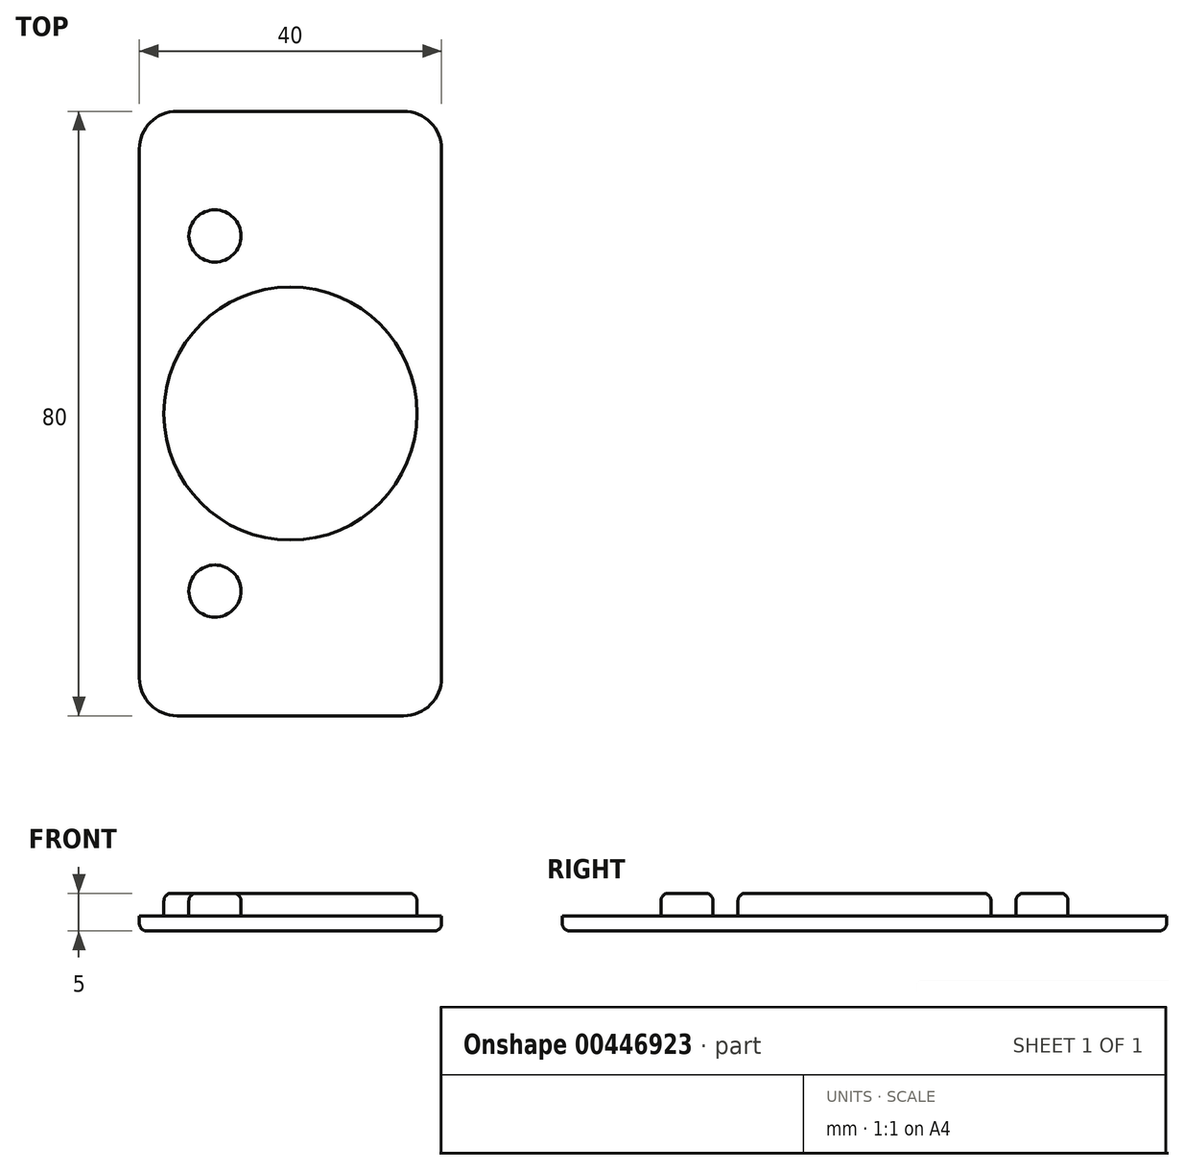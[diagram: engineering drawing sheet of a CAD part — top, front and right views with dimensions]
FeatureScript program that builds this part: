
annotation { "Feature Type Name" : "Feature", "Feature Type Description" : "" }
export const myFeature = defineFeature(function(context is Context, id is Id, definition is map)
    precondition{}
    {
        {
            var Q0;
            Q0=qCreatedBy(makeId("Top.planeOp"),FACE);
            var sketch = newSketch(context, id + "F0", { "sketchPlane" : qUnion([Q0])});
            skLineSegment(sketch, "E0.bottom", {"start": v(15, -40) * mm, "end": v(-15, -40) * mm});
            skLineSegment(sketch, "E0.top", {"start": v(15, 40) * mm, "end": v(-15, 40) * mm});
            skLineSegment(sketch, "E0.left", {"start": v(20, -35) * mm, "end": v(20, 35) * mm});
            skLineSegment(sketch, "E0.right", {"start": v(-20, -35) * mm, "end": v(-20, 35) * mm});
            skPoint(sketch, "E0.middle", {"position": v(0, 0) * mm});
            skPoint(sketch, "E1.visualSharp", {"position": v(20, -40) * mm});
            skArc(sketch, "E1.filletArc", {"start": v(15, -40) * mm, "mid": v(18.54, -38.54) * mm, "end": v(20, -35) * mm});
            skPoint(sketch, "E2.visualSharp", {"position": v(-20, -40) * mm});
            skArc(sketch, "E2.filletArc", {"start": v(-20, -35) * mm, "mid": v(-18.54, -38.54) * mm, "end": v(-15, -40) * mm});
            skPoint(sketch, "E3.visualSharp", {"position": v(-20, 40) * mm});
            skArc(sketch, "E3.filletArc", {"start": v(-15, 40) * mm, "mid": v(-18.54, 38.54) * mm, "end": v(-20, 35) * mm});
            skPoint(sketch, "E4.visualSharp", {"position": v(20, 40) * mm});
            skArc(sketch, "E4.filletArc", {"start": v(20, 35) * mm, "mid": v(18.54, 38.54) * mm, "end": v(15, 40) * mm});
            skSolve(sketch);
        }
        {
            var Q0;
            Q0=makeQuery(id+"F0.imprint","IMPRINT",FACE,{"disambiguationData":[TD([[makeQuery(id+"F0.imprint","IMPRINT",EDGE,{"derivedFrom":sQuery(id+"F0.wireOp",EDGE,"E0.bottom")}),-1.0]])]});
            extrude(context, id + "F1", {"entities" : qUnion([Q0]), "depth" : 2 * mm, "offsetDistance" : 25 * mm});
        }
        {
            var Q0;
            Q0=makeQuery(id+"F1.opExtrude","CAP_FACE",FACE,{"disambiguationData":[OSD([sQuery(id+"F0.wireOp",EDGE,"E0.bottom"),sQuery(id+"F0.wireOp",EDGE,"E0.top"),sQuery(id+"F0.wireOp",EDGE,"E0.left"),sQuery(id+"F0.wireOp",EDGE,"E0.right")])],"isStart":false});
            var sketch = newSketch(context, id + "F2", { "sketchPlane" : qUnion([Q0])});
            skCircle(sketch, "E5", {"center": v(0, 0) * mm, "radius": 17 * mm});
            skCircle(sketch, "E6", {"center": v(0, 0) * mm, "radius": 16.75 * mm});
            skLineSegment(sketch, "E7", {"start": v(0, 0) * mm, "end": v(-20, 0) * mm});
            skLineSegment(sketch, "E8", {"start": v(-20, 0) * mm, "end": v(-10, 0) * mm, "construction": true});
            skLineSegment(sketch, "E9", {"start": v(-10, -23.5) * mm, "end": v(-10, 23.5) * mm, "construction": true});
            skCircle(sketch, "E10", {"center": v(-10, -23.5) * mm, "radius": 3.7 * mm});
            skCircle(sketch, "E11", {"center": v(-10, 23.5) * mm, "radius": 3.7 * mm});
            skCircle(sketch, "E12", {"center": v(-10, -23.5) * mm, "radius": 3.45 * mm});
            skCircle(sketch, "E13", {"center": v(-10, 23.5) * mm, "radius": 3.45 * mm});
            skLineSegment(sketch, "E14", {"start": v(0, 0) * mm, "end": v(0, 40) * mm});
            skSolve(sketch);
        }
        {
            var Q0;
            Q0=makeQuery(id+"F2.imprint","IMPRINT",FACE,{"disambiguationData":[TD([[makeQuery(id+"F2.imprint","IMPRINT",EDGE,{"derivedFrom":sQuery(id+"F2.wireOp",EDGE,"E12")}),1.0]])]});
            var Q1;
            Q1=makeQuery(id+"F2.imprint","IMPRINT",FACE,{"disambiguationData":[TD([[makeQuery(id+"F2.imprint","IMPRINT",EDGE,{"derivedFrom":sQuery(id+"F2.wireOp",EDGE,"E6")}),1.0]])]});
            var Q2;
            Q2=makeQuery(id+"F2.imprint","IMPRINT",FACE,{"disambiguationData":[TD([[makeQuery(id+"F2.imprint","IMPRINT",EDGE,{"derivedFrom":sQuery(id+"F2.wireOp",EDGE,"E13")}),1.0]])]});
            extrude(context, id + "F3", {"entities" : qUnion([Q0, Q1, Q2]), "operationType" : NewBodyOperationType.ADD, "depth" : 3 * mm, "offsetDistance" : 25 * mm});
        }
        {
            var Q0;
            Q0=makeQuery(id+"F1.opExtrude","CAP_EDGE",EDGE,{"disambiguationData":[OSD([sQuery(id+"F0.wireOp",EDGE,"E0.left")])],"isStart":true});
            fillet(context, id + "F4", {"entities" : qUnion([Q0]), "radius" : 1 * mm, "tangentPropagation" : true, "allowEdgeOverflow" : false});
        }
        {
            var Q0;
            Q0=makeQuery(id+"F3.opExtrude","CAP_EDGE",EDGE,{"disambiguationData":[OSD([sQuery(id+"F2.wireOp",EDGE,"E12")])],"isStart":false});
            var Q1;
            Q1=makeQuery(id+"F3.opExtrude","CAP_FACE",FACE,{"disambiguationData":[OSD([sQuery(id+"F2.wireOp",EDGE,"E12")])],"isStart":false});
            var Q2;
            Q2=makeQuery(id+"F3.opExtrude","CAP_FACE",FACE,{"disambiguationData":[OSD([sQuery(id+"F2.wireOp",EDGE,"E6")])],"isStart":false});
            var Q3;
            Q3=makeQuery(id+"F3.opExtrude","CAP_FACE",FACE,{"disambiguationData":[OSD([sQuery(id+"F2.wireOp",EDGE,"E13")])],"isStart":false});
            fillet(context, id + "F5", {"entities" : qUnion([Q0, Q1, Q2, Q3]), "radius" : 1 * mm, "tangentPropagation" : true, "allowEdgeOverflow" : false});
        }
    });
